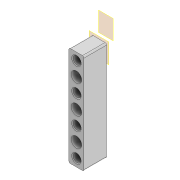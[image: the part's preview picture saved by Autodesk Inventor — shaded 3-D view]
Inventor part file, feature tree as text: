
AUTODESK INVENTOR PART (.ipt)
format: ipt  version: 2022 (Build 260153000, 153)  size: 214,016 bytes
history: native  units: mm
features: reference x12, other x6, extrude x3, sketch x3, plane x2, chamfer x2, projected_geometry x2, hole x1, fillet x1
ambient origin geometry x8: Origin, YZ Plane, XZ Plane, XY Plane, X Axis, Y Axis, Z Axis, Center Point
bodies: Volumenkörper1 (feature_tree)
feature tree (32):
  plane  "Arbeitsebene1"
  plane  "Arbeitsebene2"
  extrude  "Extrusion1"  Depth=8.0mm
  extrude  "Extrusion2"  Depth=8.0mm
  hole  "Bohrung1"  [1 undecoded]
  fillet  "Rundung1"  Radius=3.2mm
  chamfer  "Fase1"  Distance=3.2mm
  chamfer  "Fase2"  Distance=3.2mm
  extrude  "Extrusion3"  Depth=10.0mm
  sketch  "Skizze2"  dims[d0=8.0mm d1=8.0mm]
  reference  "Referenz1"
  reference  "Referenz2"
  reference  "Referenz3"
  reference  "Referenz4"
  reference  "Referenz5"
  reference  "Referenz6"
  reference  "Referenz7"
  reference  "Referenz8"
  reference  "Referenz9"
  reference  "Referenz10"
  reference  "Referenz11"
  reference  "Referenz12"
  sketch  "Skizze3"  dims[d2=8.0mm d3=8.0mm]
  projected_geometry  "Projizierte Kontur1"
  sketch  "Skizze5"  dims[d4=3.2mm d5=3.2mm d6=3.2mm d7=3.2mm d8=3.2mm d9=7.0mm d10=10.0mm d11=0.0mm d12=5.3mm d13=5.3mm d14=5.3mm d15=5.3mm d16=5.0mm d17=0.0mm d18=3.2mm d19=6.0mm d20=7.0mm d21=10.0mm d22=90.0deg d23=8.0mm d24=20.594885mm d25=2.0mm d26=0.5mm d27=2.0mm d28=45.0deg d29=1.3mm d30=2.0mm d31=45.0deg d32=1.0mm d33=10.0mm d34=0.0mm]
  projected_geometry  "Projizierte Kontur2"
  other  "Omnicscope_Xiao.iam"
  other  "00_Seeeduino Xiao:1"
  other  "00_Seeeduino Xiao:7"
  other  "00_Seeeduino Xiao:13"
  other  "Omniscope_USBC_Bar:1"
  other  "00_Seeeduino Xiao:19"
note: 1 required parameter value undecoded (feature->parameter linkage not recoverable at this tier; creation-order binding heuristic only, values carry confidence <= 0.55)
